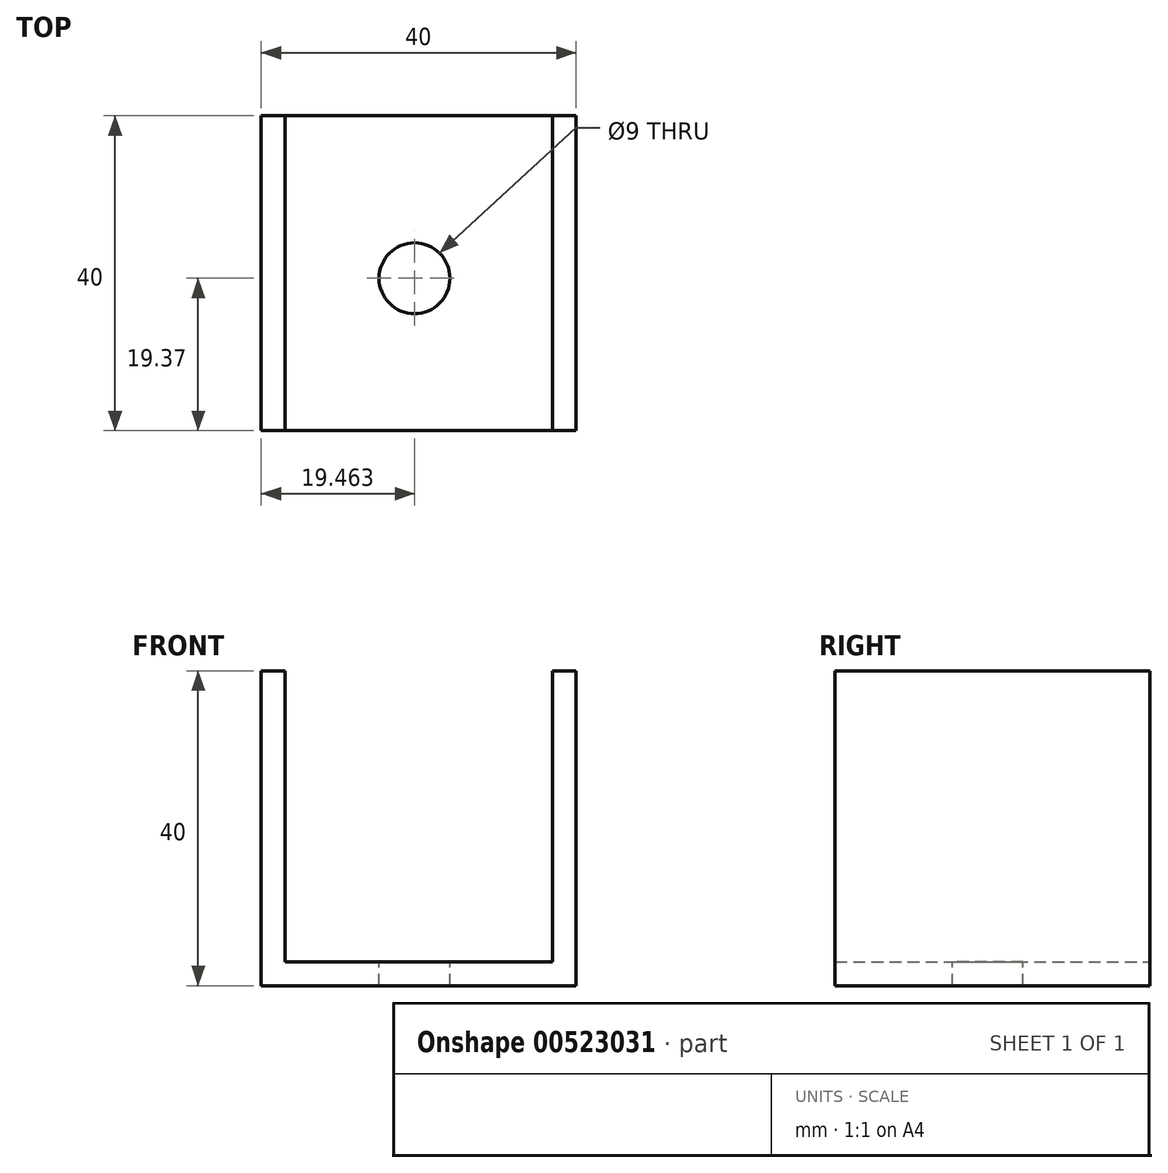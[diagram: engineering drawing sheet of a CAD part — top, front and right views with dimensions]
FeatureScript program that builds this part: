
annotation { "Feature Type Name" : "Feature", "Feature Type Description" : "" }
export const myFeature = defineFeature(function(context is Context, id is Id, definition is map)
    precondition{}
    {
        {
            var Q0;
            Q0=qCreatedBy(makeId("Front.planeOp"),FACE);
            var sketch = newSketch(context, id + "F0", { "sketchPlane" : qUnion([Q0])});
            skLineSegment(sketch, "E0", {"start": v(-22.87, -11.67) * mm, "end": v(17.13, -11.67) * mm});
            skLineSegment(sketch, "E1", {"start": v(-22.87, -11.67) * mm, "end": v(-22.87, 28.33) * mm});
            skLineSegment(sketch, "E2", {"start": v(17.13, -11.67) * mm, "end": v(17.13, 28.33) * mm});
            skLineSegment(sketch, "E3", {"start": v(-22.87, 28.33) * mm, "end": v(-19.87, 28.33) * mm});
            skLineSegment(sketch, "E4", {"start": v(17.13, 28.33) * mm, "end": v(14.13, 28.33) * mm});
            skLineSegment(sketch, "E5", {"start": v(-2.87, -8.67) * mm, "end": v(14.13, -8.67) * mm});
            skLineSegment(sketch, "E6", {"start": v(-2.87, -8.67) * mm, "end": v(-19.87, -8.67) * mm});
            skLineSegment(sketch, "E7", {"start": v(14.13, 28.33) * mm, "end": v(14.13, -8.67) * mm});
            skLineSegment(sketch, "E8", {"start": v(-19.87, -8.67) * mm, "end": v(-19.87, 28.33) * mm});
            skSolve(sketch);
        }
        {
            var Q0;
            Q0 = qSketchRegion(id + "F0", true);
            extrude(context, id + "F1", {"entities" : qUnion([Q0]), "depth" : 40 * mm, "offsetDistance" : 25 * mm});
        }
        {
            var Q0;
            Q0=makeQuery(id+"F1.opExtrude","SWEPT_FACE",FACE,{"disambiguationData":[OSD([sQuery(id+"F0.wireOp",EDGE,"E5"),sQuery(id+"F0.wireOp",EDGE,"E6")])]});
            var sketch = newSketch(context, id + "F2", { "sketchPlane" : qUnion([Q0])});
            skCircle(sketch, "E9", {"center": v(-3.4, -20.63) * mm, "radius": 4.5 * mm});
            skSolve(sketch);
        }
        {
            var Q0;
            Q0 = qSketchRegion(id + "F2", true);
            extrude(context, id + "F3", {"entities" : qUnion([Q0]), "operationType" : NewBodyOperationType.REMOVE, "oppositeDirection" : true, "depth" : 25 * mm, "offsetDistance" : 25 * mm});
        }
    });
